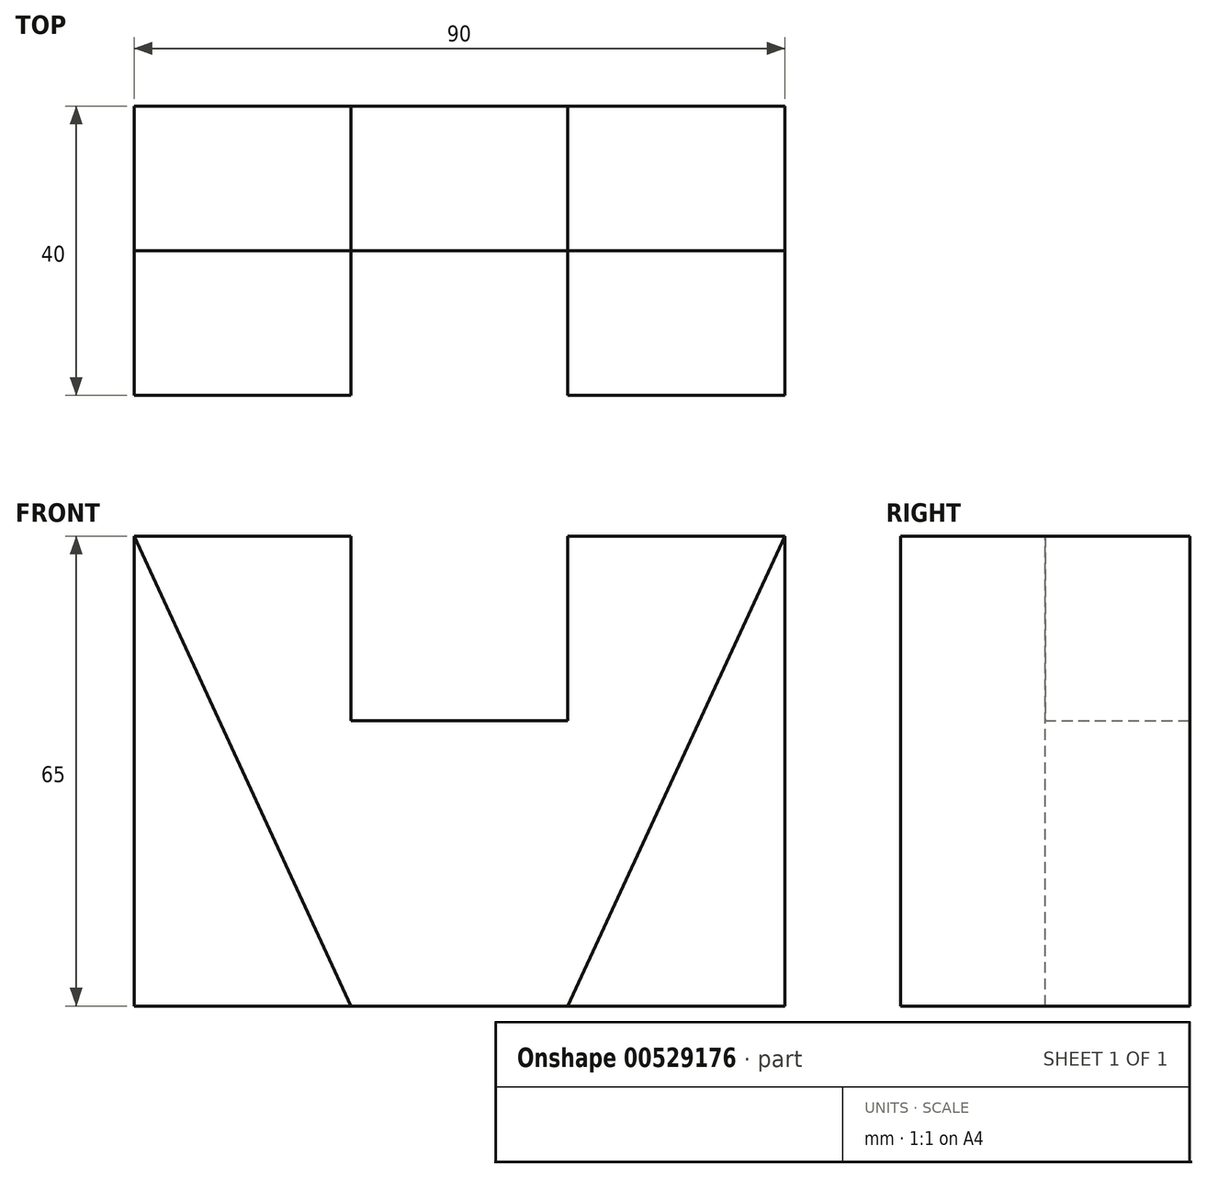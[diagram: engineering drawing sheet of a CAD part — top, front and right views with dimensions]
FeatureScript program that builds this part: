
annotation { "Feature Type Name" : "Feature", "Feature Type Description" : "" }
export const myFeature = defineFeature(function(context is Context, id is Id, definition is map)
    precondition{}
    {
        {
            var Q0;
            Q0=qCreatedBy(makeId("Front.planeOp"),FACE);
            var sketch = newSketch(context, id + "F0", { "sketchPlane" : qUnion([Q0])});
            skLineSegment(sketch, "E0.bottom", {"start": v(-54.7, 32.93) * mm, "end": v(-24.7, 32.93) * mm});
            skLineSegment(sketch, "E0.left", {"start": v(-54.7, 32.93) * mm, "end": v(-54.7, -32.07) * mm});
            skLineSegment(sketch, "E0.right", {"start": v(35.3, 32.93) * mm, "end": v(35.3, -32.07) * mm});
            skLineSegment(sketch, "E1", {"start": v(-24.7, 32.93) * mm, "end": v(-24.7, 7.39) * mm});
            skLineSegment(sketch, "E2", {"start": v(-24.7, 7.39) * mm, "end": v(5.3, 7.39) * mm});
            skLineSegment(sketch, "E3", {"start": v(5.3, 32.93) * mm, "end": v(5.3, 7.39) * mm});
            skPoint(sketch, "E4.end.orphan", {"position": v(-24.7, -32.07) * mm});
            skLineSegment(sketch, "E5", {"start": v(-54.7, -32.07) * mm, "end": v(35.3, -32.07) * mm});
            skLineSegment(sketch, "E6.trimOffspring", {"start": v(5.3, 32.93) * mm, "end": v(35.3, 32.93) * mm});
            skSolve(sketch);
        }
        {
            var Q0;
            Q0 = qSketchRegion(id + "F0", true);
            extrude(context, id + "F1", {"entities" : qUnion([Q0]), "depth" : 20 * mm, "offsetDistance" : 25 * mm});
        }
        {
            var Q0;
            Q0=makeQuery(id+"F1.opExtrude","CAP_FACE",FACE,{"disambiguationData":[OSD([sQuery(id+"F0.wireOp",EDGE,"E0.bottom"),sQuery(id+"F0.wireOp",EDGE,"E0.left"),sQuery(id+"F0.wireOp",EDGE,"E0.right"),sQuery(id+"F0.wireOp",EDGE,"E1"),sQuery(id+"F0.wireOp",EDGE,"E2"),sQuery(id+"F0.wireOp",EDGE,"E3"),sQuery(id+"F0.wireOp",EDGE,"E5"),sQuery(id+"F0.wireOp",EDGE,"E6.trimOffspring")])],"isStart":false});
            var sketch = newSketch(context, id + "F2", { "sketchPlane" : qUnion([Q0])});
            skLineSegment(sketch, "E7.top", {"start": v(-54.7, -32.07) * mm, "end": v(-24.7, -32.07) * mm});
            skLineSegment(sketch, "E7.left", {"start": v(-54.7, 32.93) * mm, "end": v(-54.7, -32.07) * mm});
            skLineSegment(sketch, "E8", {"start": v(-54.7, 32.93) * mm, "end": v(-24.7, -32.07) * mm});
            skSolve(sketch);
        }
        {
            var Q0;
            Q0 = qSketchRegion(id + "F2", true);
            extrude(context, id + "F3", {"entities" : qUnion([Q0]), "operationType" : NewBodyOperationType.ADD, "depth" : 20 * mm, "offsetDistance" : 25 * mm});
        }
        {
            var Q0;
            Q0=makeQuery(id+"F1.opExtrude","CAP_FACE",FACE,{"disambiguationData":[OSD([sQuery(id+"F0.wireOp",EDGE,"E0.bottom"),sQuery(id+"F0.wireOp",EDGE,"E0.left"),sQuery(id+"F0.wireOp",EDGE,"E0.right"),sQuery(id+"F0.wireOp",EDGE,"E1"),sQuery(id+"F0.wireOp",EDGE,"E2"),sQuery(id+"F0.wireOp",EDGE,"E3"),sQuery(id+"F0.wireOp",EDGE,"E5"),sQuery(id+"F0.wireOp",EDGE,"E6.trimOffspring")])],"isStart":false});
            var sketch = newSketch(context, id + "F4", { "sketchPlane" : qUnion([Q0])});
            skLineSegment(sketch, "E9.top", {"start": v(35.3, -32.07) * mm, "end": v(5.3, -32.07) * mm});
            skLineSegment(sketch, "E9.left", {"start": v(35.3, 32.93) * mm, "end": v(35.3, -32.07) * mm});
            skLineSegment(sketch, "E10", {"start": v(5.3, -32.07) * mm, "end": v(35.3, 32.93) * mm});
            skSolve(sketch);
        }
        {
            var Q0;
            Q0 = qSketchRegion(id + "F4", true);
            extrude(context, id + "F5", {"entities" : qUnion([Q0]), "operationType" : NewBodyOperationType.ADD, "depth" : 20 * mm, "offsetDistance" : 25 * mm});
        }
    });
